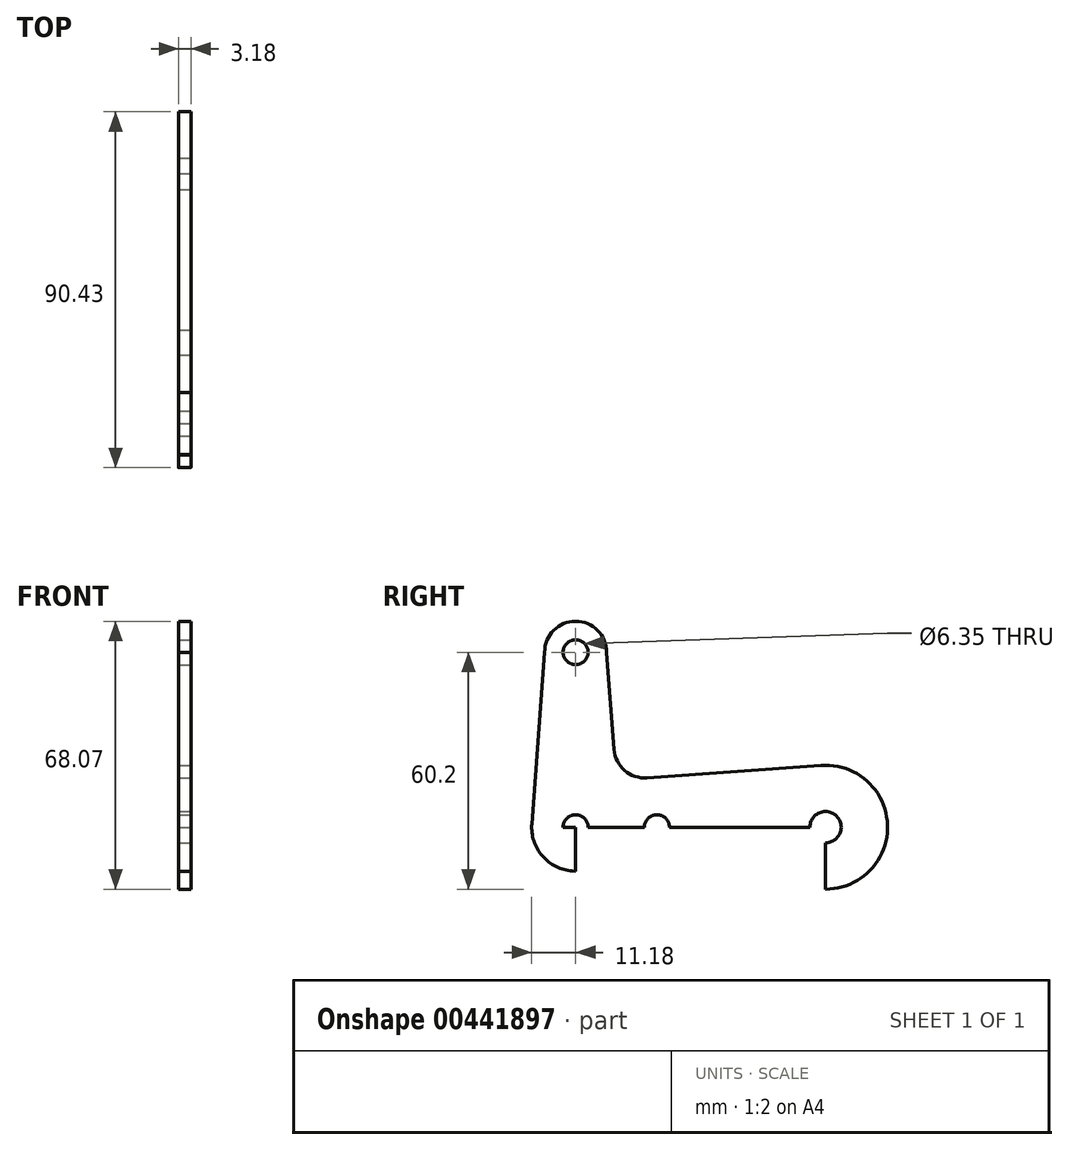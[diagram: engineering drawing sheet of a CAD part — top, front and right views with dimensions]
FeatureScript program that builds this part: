
annotation { "Feature Type Name" : "Feature", "Feature Type Description" : "" }
export const myFeature = defineFeature(function(context is Context, id is Id, definition is map)
    precondition{}
    {
        {
            var Q0;
            Q0=qCreatedBy(makeId("Right.planeOp"),FACE);
            var sketch = newSketch(context, id + "F0", { "sketchPlane" : qUnion([Q0])});
            skLineSegment(sketch, "E0", {"start": v(-14.1, 0) * mm, "end": v(82.65, 0) * mm});
            skLineSegment(sketch, "E1", {"start": v(0, -14.16) * mm, "end": v(0, 57.75) * mm});
            skLineSegment(sketch, "E2.0", {"start": v(63.5, -18.84) * mm, "end": v(63.5, 21.61) * mm});
            skArc(sketch, "E3", {"start": v(62.37, -15.7) * mm, "mid": v(79.25, 0) * mm, "end": v(62.37, 15.7) * mm});
            skArc(sketch, "E4", {"start": v(-11.15, 0.83) * mm, "mid": v(-8.46, -7.3) * mm, "end": v(-0.8, -11.15) * mm});
            skLineSegment(sketch, "E5.0", {"start": v(-11.25, 44.45) * mm, "end": v(10.57, 44.45) * mm});
            skArc(sketch, "E6", {"start": v(7.87, 44.45) * mm, "mid": v(0, 52.32) * mm, "end": v(-7.87, 44.45) * mm});
            skLineSegment(sketch, "E7", {"start": v(-7.85, 45.03) * mm, "end": v(-11.15, 0.83) * mm});
            skCircle(sketch, "E8", {"center": v(0, 0) * mm, "radius": 3.18 * mm});
            skCircle(sketch, "E9", {"center": v(63.5, 0) * mm, "radius": 3.98 * mm});
            skLineSegment(sketch, "E10", {"start": v(-0.8, -11.15) * mm, "end": v(62.37, -15.7) * mm});
            skLineSegment(sketch, "E11", {"start": v(7.85, 45.03) * mm, "end": v(9.73, 19.78) * mm});
            skArc(sketch, "E12.filletArc", {"start": v(9.73, 19.78) * mm, "mid": v(12.44, 14.4) * mm, "end": v(18.15, 12.52) * mm});
            skLineSegment(sketch, "E13", {"start": v(18.15, 12.52) * mm, "end": v(62.37, 15.7) * mm});
            skLineSegment(sketch, "E14.0", {"start": v(20.65, -4.2) * mm, "end": v(20.65, 5.6) * mm});
            skCircle(sketch, "E15", {"center": v(20.65, 0) * mm, "radius": 3.18 * mm});
            skCircle(sketch, "E16", {"center": v(0, 44.45) * mm, "radius": 3.18 * mm});
            skSolve(sketch);
        }
        {
            var Q0;
            {var subQ22=sQuery(id+"F0.wireOp",EDGE,"E12.filletArc");Q0=makeQuery(id+"F0.imprint","IMPRINT",FACE,{"disambiguationData":[TD([[makeQuery(id+"F0.imprint","IMPRINT",EDGE,{"derivedFrom":subQ22}),-1.0]])]});}
            var Q1;
            {var subQ0=sQuery(id+"F0.wireOp",EDGE,"E3");var subQ1=sQuery(id+"F0.wireOp",EDGE,"E0");var subQ2=makeQuery(id+"F0.imprint","INTERSECT",VERTEX,{"derivedFrom":[subQ1,subQ0]});Q1=makeQuery(id+"F0.imprint","IMPRINT",FACE,{"disambiguationData":[TD([[makeQuery(id+"F0.imprint","IMPRINT",EDGE,{"disambiguationData":[TD([[subQ2,1.0]])],"derivedFrom":subQ1}),1.0]])]});}
            var Q2;
            {var subQ0=sQuery(id+"F0.wireOp",EDGE,"E3");var subQ1=sQuery(id+"F0.wireOp",EDGE,"E0");var subQ2=makeQuery(id+"F0.imprint","INTERSECT",VERTEX,{"derivedFrom":[subQ1,subQ0]});Q2=makeQuery(id+"F0.imprint","IMPRINT",FACE,{"disambiguationData":[TD([[makeQuery(id+"F0.imprint","IMPRINT",EDGE,{"disambiguationData":[TD([[subQ2,1.0]])],"derivedFrom":subQ1}),-1.0]])]});}
            var Q3;
            {var subQ6=sQuery(id+"F0.wireOp",EDGE,"E0");var subQ12=sQuery(id+"F0.wireOp",EDGE,"E8");var subQ15=makeQuery(id+"F0.imprint","INTERSECT",VERTEX,{"disambiguationData":[OD(1.0)],"derivedFrom":[subQ6,subQ12]});Q3=makeQuery(id+"F0.imprint","IMPRINT",FACE,{"disambiguationData":[TD([[makeQuery(id+"F0.imprint","IMPRINT",EDGE,{"disambiguationData":[TD([[subQ15,-1.0]])],"derivedFrom":subQ6}),-1.0]])]});}
            var Q4;
            {var subQ4=sQuery(id+"F0.wireOp",EDGE,"E4");var subQ11=sQuery(id+"F0.wireOp",EDGE,"E0");var subQ12=makeQuery(id+"F0.imprint","INTERSECT",VERTEX,{"derivedFrom":[subQ11,subQ4]});Q4=makeQuery(id+"F0.imprint","IMPRINT",FACE,{"disambiguationData":[TD([[makeQuery(id+"F0.imprint","IMPRINT",EDGE,{"disambiguationData":[TD([[subQ12,-1.0]])],"derivedFrom":subQ11}),1.0]])]});}
            var Q5;
            {var subQ1=sQuery(id+"F0.wireOp",EDGE,"E0");var subQ6=sQuery(id+"F0.wireOp",EDGE,"E4");var subQ8=makeQuery(id+"F0.imprint","INTERSECT",VERTEX,{"derivedFrom":[subQ1,subQ6]});Q5=makeQuery(id+"F0.imprint","IMPRINT",FACE,{"disambiguationData":[TD([[makeQuery(id+"F0.imprint","IMPRINT",EDGE,{"disambiguationData":[TD([[subQ8,-1.0]])],"derivedFrom":subQ1}),-1.0]])]});}
            var Q6;
            {var subQ0=sQuery(id+"F0.wireOp",EDGE,"E6");var subQ2=sQuery(id+"F0.wireOp",EDGE,"E1");var subQ3=makeQuery(id+"F0.imprint","INTERSECT",VERTEX,{"derivedFrom":[subQ2,subQ0]});Q6=makeQuery(id+"F0.imprint","IMPRINT",FACE,{"disambiguationData":[TD([[makeQuery(id+"F0.imprint","IMPRINT",EDGE,{"disambiguationData":[TD([[subQ3,1.0]])],"derivedFrom":subQ2}),-1.0]])]});}
            var Q7;
            {var subQ0=sQuery(id+"F0.wireOp",EDGE,"E6");var subQ2=sQuery(id+"F0.wireOp",EDGE,"E1");var subQ3=makeQuery(id+"F0.imprint","INTERSECT",VERTEX,{"derivedFrom":[subQ2,subQ0]});Q7=makeQuery(id+"F0.imprint","IMPRINT",FACE,{"disambiguationData":[TD([[makeQuery(id+"F0.imprint","IMPRINT",EDGE,{"disambiguationData":[TD([[subQ3,1.0]])],"derivedFrom":subQ2}),1.0]])]});}
            extrude(context, id + "F1", {"entities" : qUnion([Q0, Q1, Q2, Q3, Q4, Q5, Q6, Q7]), "endBound" : BoundingType.SYMMETRIC, "oppositeDirection" : true, "depth" : 3.17 * mm});
        }
    });
